SOLIDWORKS PART (.sldprt)
format: sldprt  version: not decoded by parser v0  size: 161,792 bytes
history: native  units: mm
features: plane x12, sketch x12, cut_revolve x11, material x1, extrude x1 (+12 scaffold rows collapsed)
feature tree (49):
  scaffold x12  (default folders/planes/origin — collapsed)
  material  "Material <not specified>"
  plane  "Plane1"
  sketch  "Sketch1"
  extrude  "Boss-Extrude1"  Depth=19mm
  plane  "Plane2"
  sketch  "Sketch2"
  cut_revolve  "Cut-Revolve1"  Angle=360deg
  plane  "Plane3"
  sketch  "Sketch3"
  cut_revolve  "Cut-Revolve2"  Angle=360deg
  plane  "Plane4"
  sketch  "Sketch4"
  cut_revolve  "Cut-Revolve3"  Angle=360deg
  plane  "Plane5"
  sketch  "Sketch5"
  cut_revolve  "Cut-Revolve4"  Angle=360deg
  plane  "Plane6"
  sketch  "Sketch6"
  cut_revolve  "Cut-Revolve5"  Angle=360deg
  plane  "Plane7"
  sketch  "Sketch7"
  cut_revolve  "Cut-Revolve6"  Angle=360deg
  plane  "Plane8"
  sketch  "Sketch8"
  cut_revolve  "Cut-Revolve7"  Angle=360deg
  plane  "Plane9"
  sketch  "Sketch9"
  cut_revolve  "Cut-Revolve8"  Angle=360deg
  plane  "Plane10"
  sketch  "Sketch10"
  cut_revolve  "Cut-Revolve9"  Angle=360deg
  plane  "Plane11"
  sketch  "Sketch11"
  cut_revolve  "Cut-Revolve10"  Angle=360deg
  plane  "Plane12"
  sketch  "Sketch12"
  cut_revolve  "Cut-Revolve11"  Angle=360deg
decode coverage: 12 of 24 modeling features carry decoded parameters
note: suppression state not decoded; provenance and decode notes live in map.json
